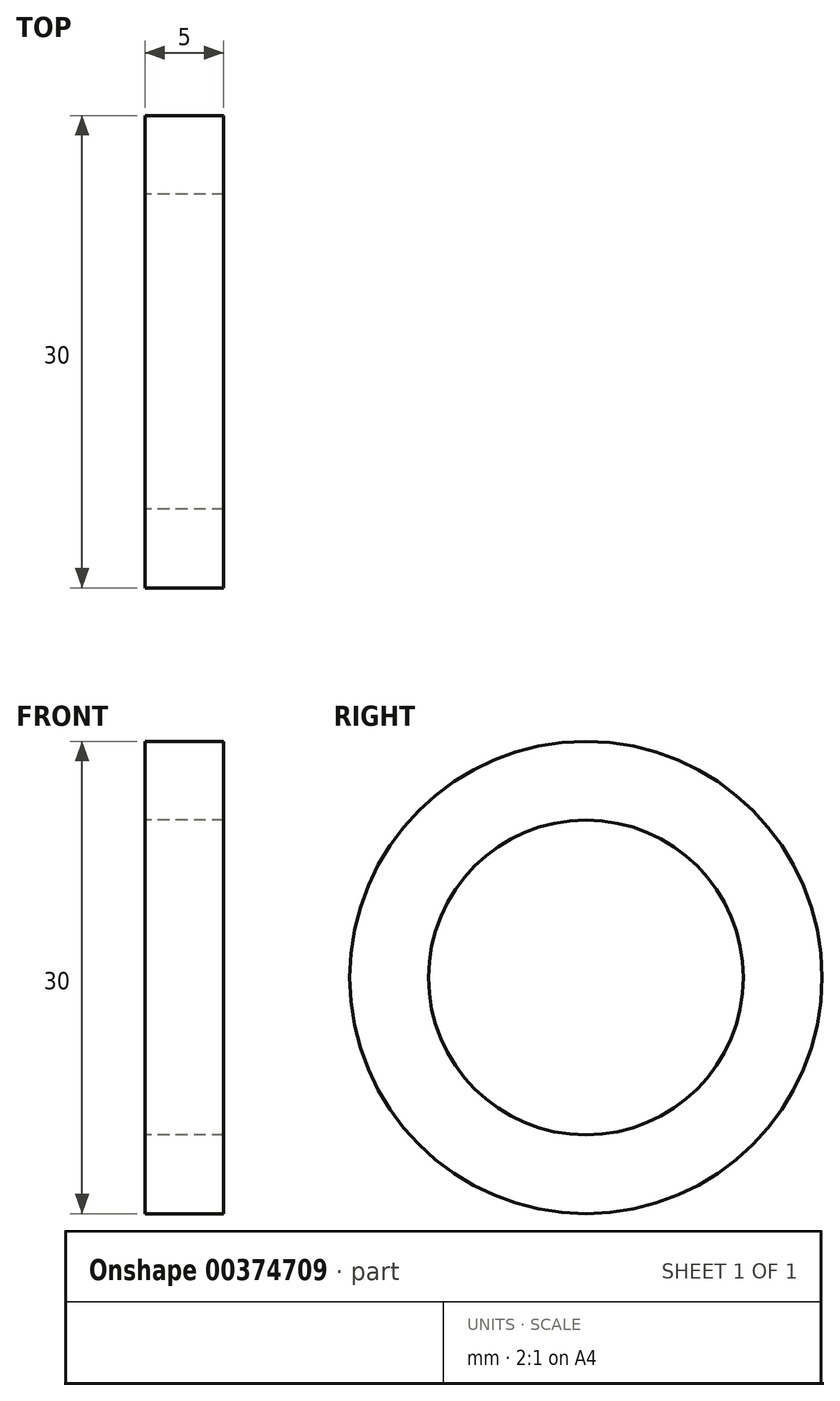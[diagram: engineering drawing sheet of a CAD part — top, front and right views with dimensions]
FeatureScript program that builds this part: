
annotation { "Feature Type Name" : "Feature", "Feature Type Description" : "" }
export const myFeature = defineFeature(function(context is Context, id is Id, definition is map)
    precondition{}
    {
        {
            var Q0;
            Q0=qCreatedBy(makeId("Right.planeOp"),FACE);
            var sketch = newSketch(context, id + "F0", { "sketchPlane" : qUnion([Q0])});
            skCircle(sketch, "E0", {"center": v(0, 0) * mm, "radius": 15 * mm});
            skCircle(sketch, "E1", {"center": v(0, 0) * mm, "radius": 10 * mm});
            skSolve(sketch);
        }
        {
            var Q0;
            Q0=makeQuery(id+"F0.imprint","IMPRINT",FACE,{"disambiguationData":[TD([[makeQuery(id+"F0.imprint","IMPRINT",EDGE,{"derivedFrom":sQuery(id+"F0.wireOp",EDGE,"E0")}),1.0]])]});
            extrude(context, id + "F1", {"entities" : qUnion([Q0]), "endBound" : BoundingType.SYMMETRIC, "depth" : 5 * mm});
        }
    });
